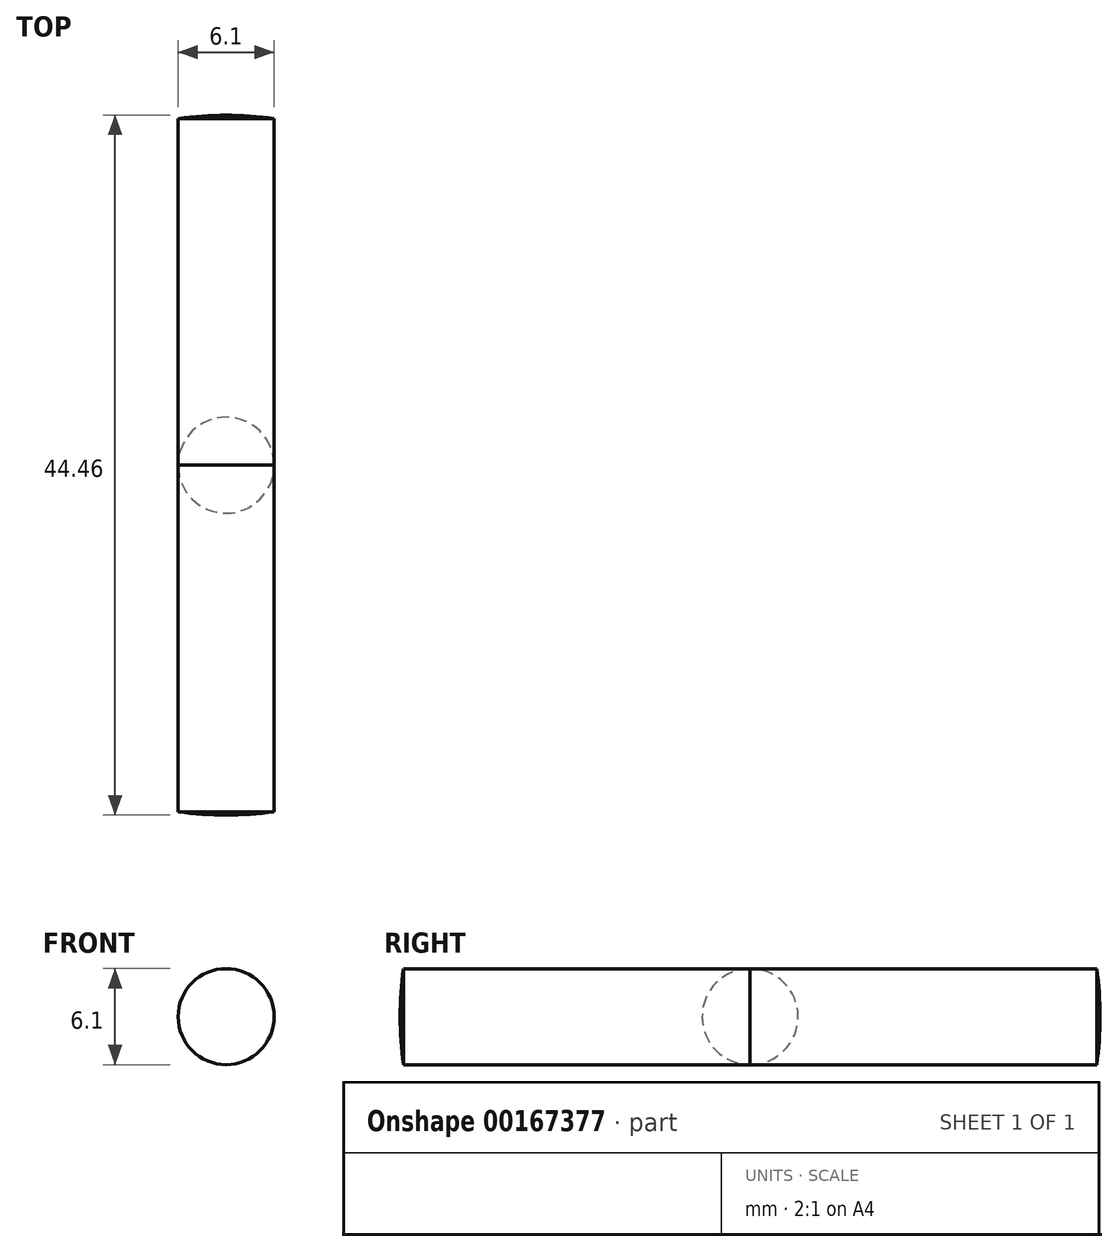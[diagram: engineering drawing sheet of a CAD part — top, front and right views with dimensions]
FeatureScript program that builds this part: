
annotation { "Feature Type Name" : "Feature", "Feature Type Description" : "" }
export const myFeature = defineFeature(function(context is Context, id is Id, definition is map)
    precondition{}
    {
        {
            var Q0;
            Q0=qCreatedBy(makeId("Front.planeOp"),FACE);
            var sketch = newSketch(context, id + "F0", { "sketchPlane" : qUnion([Q0])});
            skCircle(sketch, "E0", {"center": v(0, 0) * mm, "radius": 22.23 * mm});
            skLineSegment(sketch, "E1", {"start": v(0, 22.23) * mm, "end": v(0, -22.23) * mm});
            skCircle(sketch, "E2", {"center": v(0, 0) * mm, "radius": 3.05 * mm});
            skSolve(sketch);
        }
        {
            var Q0;
            {var subQ0=sQuery(id+"F0.wireOp",EDGE,"E1");Q0=makeQuery(id+"F0.imprint","IMPRINT",FACE,{"disambiguationData":[TD([[makeQuery(id+"F0.imprint","IMPRINT",EDGE,{"derivedFrom":subQ0}),1.0]])]});}
            var Q1;
            Q1=sQuery(id+"F0.wireOp",EDGE,"E1");
            revolve(context, id + "F1", {"entities" : qUnion([Q0]), "axis" : qUnion([Q1]), "revolveType" : RevolveType.FULL});
        }
        {
            var Q0;
            {var subQ0=sQuery(id+"F0.wireOp",EDGE,"E2");var subQ1=sQuery(id+"F0.wireOp",EDGE,"E1");var subQ2=makeQuery(id+"F0.imprint","INTERSECT",VERTEX,{"disambiguationData":[OD(0.0)],"derivedFrom":[subQ1,subQ0]});Q0=makeQuery(id+"F0.imprint","IMPRINT",FACE,{"disambiguationData":[TD([[makeQuery(id+"F0.imprint","IMPRINT",EDGE,{"disambiguationData":[TD([[subQ2,-1.0]])],"derivedFrom":subQ1}),1.0]])]});}
            var Q1;
            {var subQ0=sQuery(id+"F0.wireOp",EDGE,"E2");var subQ1=sQuery(id+"F0.wireOp",EDGE,"E1");var subQ2=makeQuery(id+"F0.imprint","INTERSECT",VERTEX,{"disambiguationData":[OD(0.0)],"derivedFrom":[subQ1,subQ0]});Q1=makeQuery(id+"F0.imprint","IMPRINT",FACE,{"disambiguationData":[TD([[makeQuery(id+"F0.imprint","IMPRINT",EDGE,{"disambiguationData":[TD([[subQ2,-1.0]])],"derivedFrom":subQ1}),-1.0]])]});}
            extrude(context, id + "F2", {"entities" : qUnion([Q0, Q1]), "operationType" : NewBodyOperationType.REMOVE, "depth" : 25.4 * mm});
        }
        {
            var Q0;
            {var subQ0=sQuery(id+"F0.wireOp",EDGE,"E2");var subQ1=sQuery(id+"F0.wireOp",EDGE,"E1");var subQ2=makeQuery(id+"F0.imprint","INTERSECT",VERTEX,{"disambiguationData":[OD(0.0)],"derivedFrom":[subQ1,subQ0]});Q0=makeQuery(id+"F0.imprint","IMPRINT",FACE,{"disambiguationData":[TD([[makeQuery(id+"F0.imprint","IMPRINT",EDGE,{"disambiguationData":[TD([[subQ2,-1.0]])],"derivedFrom":subQ1}),-1.0]])]});}
            var Q1;
            {var subQ0=sQuery(id+"F0.wireOp",EDGE,"E2");var subQ1=sQuery(id+"F0.wireOp",EDGE,"E1");var subQ2=makeQuery(id+"F0.imprint","INTERSECT",VERTEX,{"disambiguationData":[OD(0.0)],"derivedFrom":[subQ1,subQ0]});Q1=makeQuery(id+"F0.imprint","IMPRINT",FACE,{"disambiguationData":[TD([[makeQuery(id+"F0.imprint","IMPRINT",EDGE,{"disambiguationData":[TD([[subQ2,-1.0]])],"derivedFrom":subQ1}),1.0]])]});}
            extrude(context, id + "F3", {"entities" : qUnion([Q0, Q1]), "operationType" : NewBodyOperationType.REMOVE, "oppositeDirection" : true, "depth" : 25.4 * mm});
        }
    });
